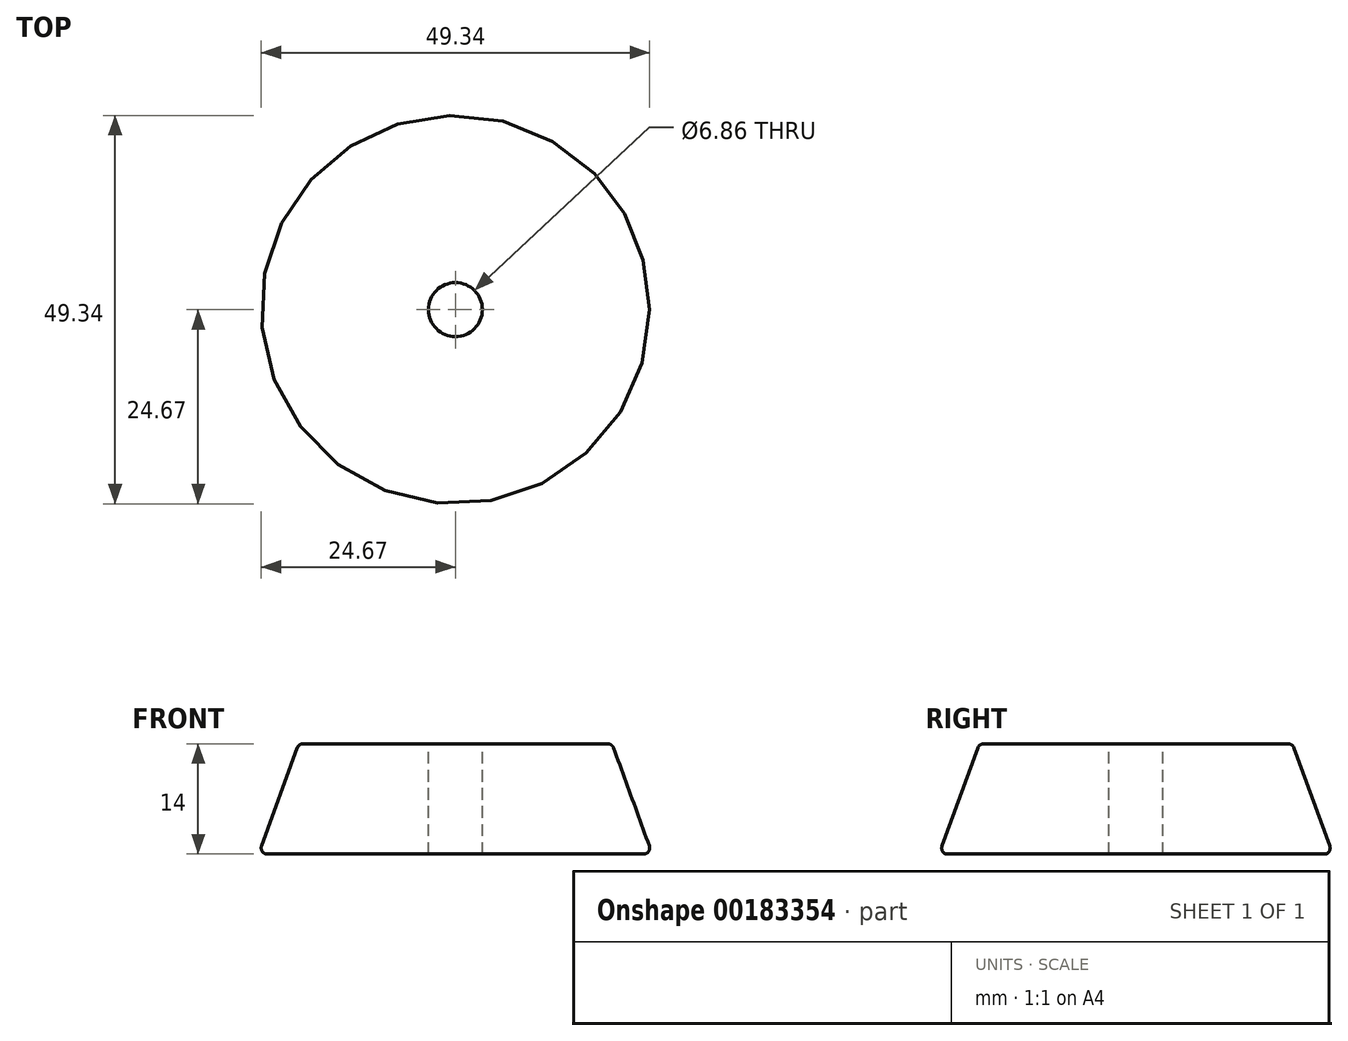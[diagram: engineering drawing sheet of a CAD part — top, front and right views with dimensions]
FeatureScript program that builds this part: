
annotation { "Feature Type Name" : "Feature", "Feature Type Description" : "" }
export const myFeature = defineFeature(function(context is Context, id is Id, definition is map)
    precondition{}
    {
        {
            var Q0;
            Q0=qCreatedBy(makeId("Top.planeOp"),FACE);
            var sketch = newSketch(context, id + "F0", { "sketchPlane" : qUnion([Q0])});
            skCircle(sketch, "E0", {"center": v(0, 0) * mm, "radius": 25 * mm});
            skSolve(sketch);
        }
        {
            var Q0;
            Q0 = qSketchRegion(id + "F0", true);
            extrude(context, id + "F1", {"entities" : qUnion([Q0]), "depth" : 14 * mm, "hasDraft" : true, "draftAngle" : 20 * degree, "draftPullDirection" : true});
        }
        {
            var Q0;
            Q0=makeQuery(id+"F1.opExtrude","CAP_FACE",FACE,{"disambiguationData":[OSD([sQuery(id+"F0.wireOp",EDGE,"E0")])],"isStart":false});
            var sketch = newSketch(context, id + "F2", { "sketchPlane" : qUnion([Q0])});
            skPoint(sketch, "E1", {"position": v(0, 0) * mm});
            skSolve(sketch);
        }
        {
            var Q0;
            Q0=sQuery(id+"F2.wireOp",VERTEX,"E1");
            var Q1;
            Q1=makeQuery(id+"F1.opExtrude","SWEPT_BODY",BODY,{"disambiguationData":[OSD([sQuery(id+"F0.wireOp",EDGE,"E0")])]});
            hole(context, id + "F3", {"style" : HoleStyle.SIMPLE, "endStyle" : HoleEndStyle.THROUGH, "holeDiameter" : 6.86 * mm, "locations" : qUnion([Q0]), "scope" : qUnion([Q1]), "isTappedThrough" : true});
        }
        {
            var Q0;
            Q0=makeQuery(id+"F1.opExtrude","CAP_EDGE",EDGE,{"disambiguationData":[OSD([sQuery(id+"F0.wireOp",EDGE,"E0")])],"isStart":false});
            var Q1;
            Q1=makeQuery(id+"F1.opExtrude","CAP_EDGE",EDGE,{"disambiguationData":[OSD([sQuery(id+"F0.wireOp",EDGE,"E0")])],"isStart":true});
            fillet(context, id + "F4", {"entities" : qUnion([Q0, Q1]), "radius" : 0.76 * mm, "tangentPropagation" : true, "allowEdgeOverflow" : false});
        }
    });
